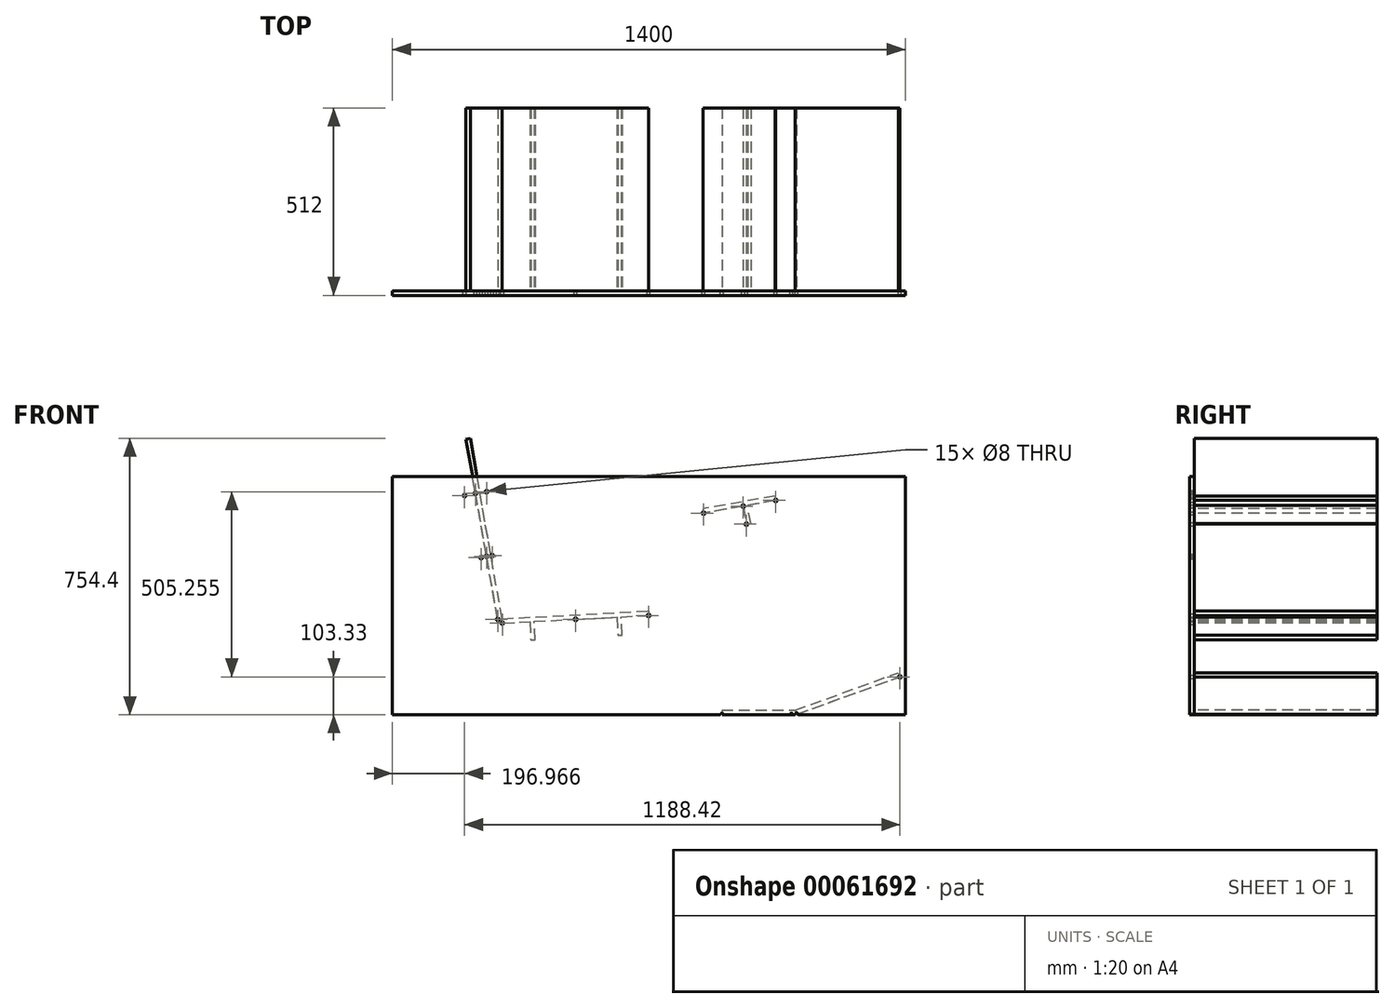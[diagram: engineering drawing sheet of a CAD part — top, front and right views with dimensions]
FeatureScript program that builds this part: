
annotation { "Feature Type Name" : "Feature", "Feature Type Description" : "" }
export const myFeature = defineFeature(function(context is Context, id is Id, definition is map)
    precondition{}
    {
        {
            var Q0;
            Q0=qCreatedBy(makeId("Front.planeOp"),FACE);
            var sketch = newSketch(context, id + "F0", { "sketchPlane" : qUnion([Q0])});
            skLineSegment(sketch, "E0.bottom", {"start": v(0, 0) * mm, "end": v(-11.82, -2.08) * mm});
            skLineSegment(sketch, "E0.top", {"start": v(-86.82, 492.4) * mm, "end": v(-98.64, 490.32) * mm});
            skLineSegment(sketch, "E0.left", {"start": v(0, 0) * mm, "end": v(-86.82, 492.4) * mm});
            skLineSegment(sketch, "E0.right", {"start": v(-11.82, -2.08) * mm, "end": v(-98.64, 490.32) * mm});
            skLineSegment(sketch, "E1.bottom", {"start": v(600, -250) * mm, "end": v(800, -250) * mm});
            skLineSegment(sketch, "E1.top", {"start": v(600, -262) * mm, "end": v(800, -262) * mm});
            skLineSegment(sketch, "E1.left", {"start": v(600, -250) * mm, "end": v(600, -262) * mm});
            skLineSegment(sketch, "E1.right", {"start": v(800, -250) * mm, "end": v(800, -262) * mm});
            skLineSegment(sketch, "E2.bottom", {"start": v(800, -250) * mm, "end": v(804.1, -261.28) * mm});
            skLineSegment(sketch, "E2.top", {"start": v(1081.9, -147.4) * mm, "end": v(1086.01, -158.67) * mm});
            skLineSegment(sketch, "E2.left", {"start": v(800, -250) * mm, "end": v(1081.9, -147.4) * mm});
            skLineSegment(sketch, "E2.right", {"start": v(804.1, -261.28) * mm, "end": v(1086.01, -158.67) * mm});
            skLineSegment(sketch, "E3.bottom", {"start": v(744.88, 334.73) * mm, "end": v(746.96, 322.91) * mm});
            skLineSegment(sketch, "E3.top", {"start": v(547.92, 300) * mm, "end": v(550, 288.18) * mm});
            skLineSegment(sketch, "E3.left", {"start": v(744.88, 334.73) * mm, "end": v(547.92, 300) * mm});
            skLineSegment(sketch, "E3.right", {"start": v(746.96, 322.91) * mm, "end": v(550, 288.18) * mm});
            skLineSegment(sketch, "E4", {"start": v(0, 0) * mm, "end": v(0, 206.93) * mm});
            skLineSegment(sketch, "E5.bottom", {"start": v(0, 0) * mm, "end": v(399.45, 20.93) * mm});
            skLineSegment(sketch, "E5.top", {"start": v(0.63, -11.98) * mm, "end": v(400.08, 8.95) * mm});
            skLineSegment(sketch, "E5.left", {"start": v(0, 0) * mm, "end": v(0.63, -11.98) * mm});
            skLineSegment(sketch, "E5.right", {"start": v(399.45, 20.93) * mm, "end": v(400.08, 8.95) * mm});
            skLineSegment(sketch, "E6", {"start": v(658.33, 307.28) * mm, "end": v(667.01, 258.04) * mm});
            skLineSegment(sketch, "E7", {"start": v(667.01, 258.04) * mm, "end": v(678.83, 260.13) * mm});
            skLineSegment(sketch, "E8", {"start": v(678.83, 260.13) * mm, "end": v(670.15, 309.37) * mm});
            skLineSegment(sketch, "E9", {"start": v(75.53, -8.06) * mm, "end": v(78.14, -57.99) * mm});
            skLineSegment(sketch, "E10", {"start": v(78.14, -57.99) * mm, "end": v(90.13, -57.36) * mm});
            skLineSegment(sketch, "E11", {"start": v(90.13, -57.36) * mm, "end": v(87.5, -7.43) * mm});
            skLineSegment(sketch, "E12", {"start": v(313.2, 4.4) * mm, "end": v(315.82, -45.53) * mm});
            skLineSegment(sketch, "E13", {"start": v(315.82, -45.53) * mm, "end": v(327.8, -44.9) * mm});
            skLineSegment(sketch, "E14", {"start": v(327.8, -44.9) * mm, "end": v(325.18, 5.03) * mm});
            skSolve(sketch);
        }
        {
            var Q0;
            Q0=makeQuery(id+"F0.imprint","IMPRINT",FACE,{"disambiguationData":[TD([[makeQuery(id+"F0.imprint","IMPRINT",EDGE,{"derivedFrom":sQuery(id+"F0.wireOp",EDGE,"E0.bottom")}),-1.0]])]});
            var Q1;
            Q1=makeQuery(id+"F0.imprint","IMPRINT",FACE,{"disambiguationData":[TD([[makeQuery(id+"F0.imprint","IMPRINT",EDGE,{"derivedFrom":sQuery(id+"F0.wireOp",EDGE,"E5.bottom")}),-1.0]])]});
            var Q2;
            Q2=makeQuery(id+"F0.imprint","IMPRINT",FACE,{"disambiguationData":[TD([[makeQuery(id+"F0.imprint","IMPRINT",EDGE,{"derivedFrom":sQuery(id+"F0.wireOp",EDGE,"E3.bottom")}),-1.0]])]});
            var Q3;
            Q3=makeQuery(id+"F0.imprint","IMPRINT",FACE,{"disambiguationData":[TD([[makeQuery(id+"F0.imprint","IMPRINT",EDGE,{"derivedFrom":sQuery(id+"F0.wireOp",EDGE,"E1.bottom")}),-1.0]])]});
            var Q4;
            Q4=makeQuery(id+"F0.imprint","IMPRINT",FACE,{"disambiguationData":[TD([[makeQuery(id+"F0.imprint","IMPRINT",EDGE,{"derivedFrom":sQuery(id+"F0.wireOp",EDGE,"E2.bottom")}),1.0]])]});
            var Q5;
            {var subQ0=sQuery(id+"F0.wireOp",EDGE,"E6");Q5=makeQuery(id+"F0.imprint","IMPRINT",FACE,{"disambiguationData":[TD([[makeQuery(id+"F0.imprint","IMPRINT",EDGE,{"derivedFrom":subQ0}),1.0]])]});}
            var Q6;
            {var subQ0=sQuery(id+"F0.wireOp",EDGE,"E9");Q6=makeQuery(id+"F0.imprint","IMPRINT",FACE,{"disambiguationData":[TD([[makeQuery(id+"F0.imprint","IMPRINT",EDGE,{"derivedFrom":subQ0}),1.0]])]});}
            var Q7;
            {var subQ0=sQuery(id+"F0.wireOp",EDGE,"E12");Q7=makeQuery(id+"F0.imprint","IMPRINT",FACE,{"disambiguationData":[TD([[makeQuery(id+"F0.imprint","IMPRINT",EDGE,{"derivedFrom":subQ0}),1.0]])]});}
            extrude(context, id + "F1", {"entities" : qUnion([Q0, Q1, Q2, Q3, Q4, Q5, Q6, Q7]), "oppositeDirection" : true, "depth" : 500 * mm});
        }
        {
            var Q0;
            Q0=qCreatedBy(makeId("Front.planeOp"),FACE);
            var sketch = newSketch(context, id + "F2", { "sketchPlane" : qUnion([Q0])});
            skLineSegment(sketch, "E15.bottom", {"start": v(1100.63, -262) * mm, "end": v(-299.37, -262) * mm});
            skLineSegment(sketch, "E15.top", {"start": v(1100.63, 388) * mm, "end": v(-299.37, 388) * mm});
            skLineSegment(sketch, "E15.left", {"start": v(1100.63, -262) * mm, "end": v(1100.63, 388) * mm});
            skLineSegment(sketch, "E15.right", {"start": v(-299.37, -262) * mm, "end": v(-299.37, 388) * mm});
            skCircle(sketch, "E16", {"center": v(200.63, -1.5) * mm, "radius": 4 * mm});
            skCircle(sketch, "E17", {"center": v(400.08, 8.95) * mm, "radius": 4 * mm});
            skCircle(sketch, "E18", {"center": v(550, 288.18) * mm, "radius": 4 * mm});
            skCircle(sketch, "E19", {"center": v(746.96, 322.91) * mm, "radius": 4 * mm});
            skCircle(sketch, "E20", {"center": v(600, -262) * mm, "radius": 4 * mm});
            skCircle(sketch, "E21", {"center": v(804.1, -261.28) * mm, "radius": 4 * mm});
            skCircle(sketch, "E22", {"center": v(1086.01, -158.67) * mm, "radius": 4 * mm});
            skCircle(sketch, "E23", {"center": v(790, -262) * mm, "radius": 4 * mm});
            skCircle(sketch, "E24", {"center": v(-72.6, 342.6) * mm, "radius": 4 * mm});
            skLineSegment(sketch, "E25", {"start": v(-11.82, -2.08) * mm, "end": v(-42.32, 346.58) * mm});
            skCircle(sketch, "E26", {"center": v(-42.32, 346.58) * mm, "radius": 4 * mm});
            skLineSegment(sketch, "E27", {"start": v(-11.82, -2.08) * mm, "end": v(-102.4, 336) * mm});
            skCircle(sketch, "E28", {"center": v(-102.4, 336) * mm, "radius": 4 * mm});
            skCircle(sketch, "E29", {"center": v(0.63, -11.98) * mm, "radius": 4 * mm});
            skCircle(sketch, "E30", {"center": v(-11.82, -2.08) * mm, "radius": 4 * mm});
            skCircle(sketch, "E31", {"center": v(667.01, 258.04) * mm, "radius": 4 * mm});
            skCircle(sketch, "E32", {"center": v(658.33, 307.28) * mm, "radius": 4 * mm});
            skCircle(sketch, "E33", {"center": v(-27.07, 172.25) * mm, "radius": 4 * mm});
            skCircle(sketch, "E34", {"center": v(-57.11, 166.95) * mm, "radius": 4 * mm});
            skCircle(sketch, "E35", {"center": v(-42.2, 170.26) * mm, "radius": 4 * mm});
            skSolve(sketch);
        }
        {
            var Q0;
            Q0=makeQuery(id+"F2.imprint","IMPRINT",FACE,{"disambiguationData":[TD([[makeQuery(id+"F2.imprint","IMPRINT",EDGE,{"derivedFrom":sQuery(id+"F2.wireOp",EDGE,"E15.bottom")}),-1.0]])]});
            extrude(context, id + "F3", {"entities" : qUnion([Q0]), "depth" : 12 * mm});
        }
        {
            var Q0;
            Q0=makeQuery(id+"F1.opExtrude","CAP_FACE",FACE,{"disambiguationData":[OSD([sQuery(id+"F0.wireOp",EDGE,"E5.bottom"),sQuery(id+"F0.wireOp",EDGE,"E5.top"),sQuery(id+"F0.wireOp",EDGE,"E5.left"),sQuery(id+"F0.wireOp",EDGE,"E5.right")])],"isStart":false});
            cPlane(context, id + "F4", {"entities" : qUnion([Q0]), "cplaneType" : CPlaneType.OFFSET, "offset" : 0 * mm, "width" : 150 * mm, "height" : 150 * mm});
        }
    });
